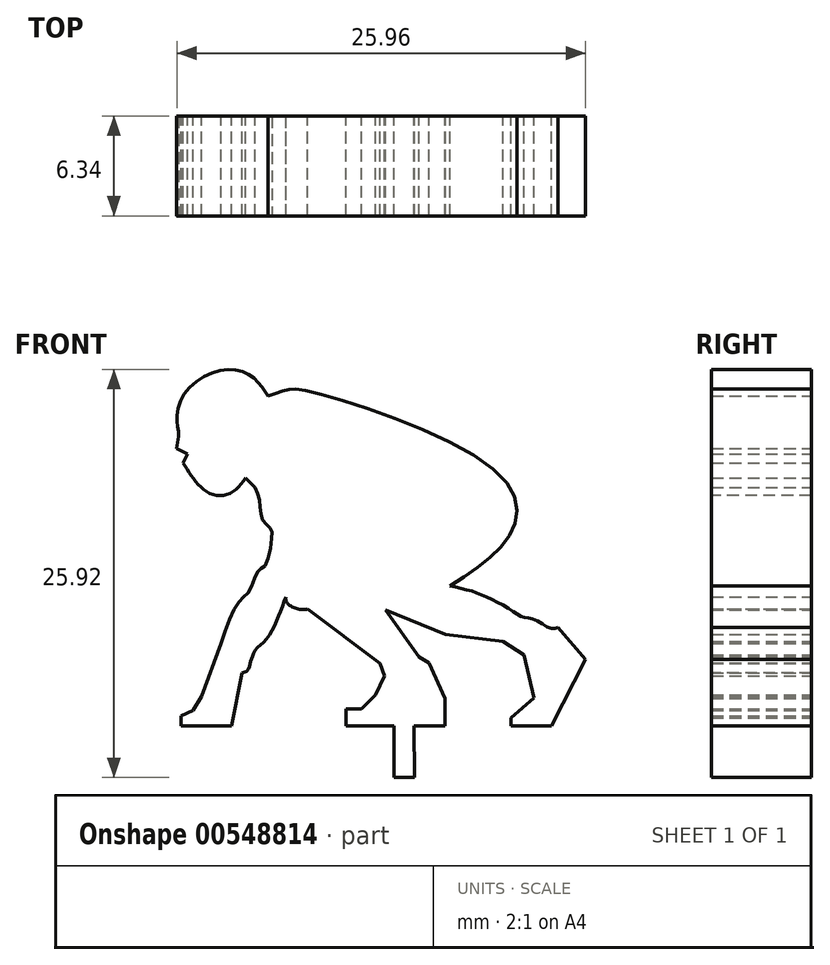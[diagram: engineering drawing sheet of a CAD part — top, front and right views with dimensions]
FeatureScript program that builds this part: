
annotation { "Feature Type Name" : "Feature", "Feature Type Description" : "" }
export const myFeature = defineFeature(function(context is Context, id is Id, definition is map)
    precondition{}
    {
        {
            var Q0;
            Q0=qCreatedBy(makeId("Front.planeOp"),FACE);
            var sketch = newSketch(context, id + "F0", { "sketchPlane" : qUnion([Q0])});
            skLineSegment(sketch, "E0", {"start": v(-11.37, -3.27) * mm, "end": v(-12.65, -3.27) * mm});
            skLineSegment(sketch, "E1", {"start": v(-12.65, -3.27) * mm, "end": v(-12.65, 0) * mm});
            skLineSegment(sketch, "E2", {"start": v(-12.65, 0) * mm, "end": v(-15.72, 0) * mm});
            skLineSegment(sketch, "E3", {"start": v(-15.72, 0) * mm, "end": v(-15.72, 1.09) * mm});
            skLineSegment(sketch, "E4", {"start": v(-15.72, 1.09) * mm, "end": v(-14.7, 1.09) * mm});
            skLineSegment(sketch, "E5", {"start": v(-14.7, 1.09) * mm, "end": v(-13.85, 1.97) * mm});
            skLineSegment(sketch, "E6", {"start": v(-13.85, 1.97) * mm, "end": v(-13.28, 3.19) * mm});
            skLineSegment(sketch, "E7", {"start": v(-13.28, 3.19) * mm, "end": v(-13.55, 3.98) * mm});
            skLineSegment(sketch, "E8", {"start": v(-13.55, 3.98) * mm, "end": v(-18.14, 7.43) * mm});
            skFitSpline(sketch, "E9", {"points": [v(-18.14, 7.43) * mm, v(-18.74, 7.43) * mm, v(-19.46, 7.83) * mm, v(-19.53, 8.2) * mm], "startDerivative": vector(-1.65, -0.23) * mm, "endDerivative": vector(0.09, 1.4) * mm});
            skFitSpline(sketch, "E10", {"points": [v(-19.53, 8.2) * mm, v(-20.08, 6.77) * mm, v(-20.8, 5.46) * mm, v(-21.47, 4.8) * mm, v(-21.7, 4.27) * mm, v(-21.82, 3.9) * mm, v(-21.97, 3.51) * mm, v(-22.32, 3.38) * mm, v(-22.32, 3.4) * mm], "startDerivative": vector(-2.6, -7.11) * mm, "endDerivative": vector(0.45, 1.13) * mm});
            skLineSegment(sketch, "E11", {"start": v(-22.32, 3.38) * mm, "end": v(-22.99, 0) * mm});
            skLineSegment(sketch, "E12", {"start": v(-22.99, 0) * mm, "end": v(-26.18, 0) * mm});
            skLineSegment(sketch, "E13", {"start": v(-26.18, 0) * mm, "end": v(-26.18, 0.65) * mm});
            skLineSegment(sketch, "E14", {"start": v(-26.18, 0.65) * mm, "end": v(-25.42, 1) * mm});
            skLineSegment(sketch, "E15", {"start": v(-25.42, 1) * mm, "end": v(-24.9, 1.86) * mm});
            skLineSegment(sketch, "E16", {"start": v(-24.9, 1.86) * mm, "end": v(-23.65, 5.23) * mm});
            skFitSpline(sketch, "E17", {"points": [v(-23.65, 5.23) * mm, v(-22.48, 7.91) * mm, v(-21.8, 8.6) * mm, v(-21.28, 9.87) * mm, v(-20.88, 10.15) * mm, v(-20.4, 12.04) * mm, v(-20.54, 12.6) * mm, v(-21.02, 13.11) * mm, v(-21.18, 14.2) * mm, v(-21.48, 15.15) * mm], "startDerivative": vector(6.31, 18.33) * mm, "endDerivative": vector(-3.63, 8.71) * mm});
            skLineSegment(sketch, "E18", {"start": v(-21.48, 15.15) * mm, "end": v(-22.08, 15.75) * mm});
            skFitSpline(sketch, "E19", {"points": [v(-22.08, 15.75) * mm, v(-23.04, 14.79) * mm, v(-24.22, 14.71) * mm, v(-25.25, 15.54) * mm, v(-26.07, 16.71) * mm], "startDerivative": vector(-3.44, -4.51) * mm, "endDerivative": vector(-2.96, 4.64) * mm});
            skLineSegment(sketch, "E20", {"start": v(-26.07, 16.71) * mm, "end": v(-25.78, 17.27) * mm});
            skLineSegment(sketch, "E21", {"start": v(-25.78, 17.27) * mm, "end": v(-26.45, 17.62) * mm});
            skFitSpline(sketch, "E22", {"points": [v(-26.45, 17.62) * mm, v(-26.35, 18.68) * mm, v(-26.45, 19.5) * mm, v(-25.96, 21.1) * mm, v(-24.04, 22.5) * mm, v(-22.23, 22.5) * mm, v(-21.22, 21.75) * mm, v(-20.66, 20.95) * mm], "startDerivative": vector(1.41, 8.93) * mm, "endDerivative": vector(4.2, -6.65) * mm});
            skFitSpline(sketch, "E23", {"points": [v(-20.66, 20.95) * mm, v(-19.54, 21.34) * mm, v(-18.14, 21.27) * mm, v(-5.9, 15.92) * mm, v(-5.29, 12.16) * mm, v(-9.11, 8.9) * mm], "startDerivative": vector(11.08, 4.16) * mm, "endDerivative": vector(-20.81, -13.46) * mm});
            skFitSpline(sketch, "E24", {"points": [v(-9.11, 8.9) * mm, v(-7.8, 8.58) * mm, v(-6.7, 8.15) * mm, v(-5.28, 7.41) * mm, v(-4.5, 6.92) * mm, v(-3.8, 6.79) * mm, v(-2.72, 6.21) * mm, v(-2.24, 6.27) * mm], "startDerivative": vector(8.42, -1.68) * mm, "endDerivative": vector(4.44, 1.66) * mm});
            skLineSegment(sketch, "E25", {"start": v(-2.24, 6.27) * mm, "end": v(-0.49, 4.22) * mm});
            skLineSegment(sketch, "E26", {"start": v(-0.49, 4.22) * mm, "end": v(-2.64, 0) * mm});
            skLineSegment(sketch, "E27", {"start": v(-2.64, 0) * mm, "end": v(-5.23, 0) * mm});
            skLineSegment(sketch, "E28", {"start": v(-5.23, 0) * mm, "end": v(-5.23, 0.52) * mm});
            skLineSegment(sketch, "E29", {"start": v(-5.23, 0.52) * mm, "end": v(-3.78, 1.8) * mm});
            skLineSegment(sketch, "E30", {"start": v(-3.78, 1.8) * mm, "end": v(-4.4, 4.52) * mm});
            skLineSegment(sketch, "E31", {"start": v(-4.4, 4.52) * mm, "end": v(-5.73, 5.37) * mm});
            skLineSegment(sketch, "E32", {"start": v(-5.73, 5.37) * mm, "end": v(-9.39, 5.8) * mm});
            skLineSegment(sketch, "E33", {"start": v(-9.39, 5.8) * mm, "end": v(-13.19, 7.39) * mm});
            skLineSegment(sketch, "E34", {"start": v(-13.19, 7.39) * mm, "end": v(-11.09, 4.39) * mm});
            skLineSegment(sketch, "E35", {"start": v(-11.09, 4.39) * mm, "end": v(-10.45, 4) * mm});
            skLineSegment(sketch, "E36", {"start": v(-10.45, 4) * mm, "end": v(-9.43, 1.74) * mm});
            skLineSegment(sketch, "E37", {"start": v(-9.43, 1.74) * mm, "end": v(-9.43, 0) * mm});
            skLineSegment(sketch, "E38", {"start": v(-9.43, 0) * mm, "end": v(-11.37, 0) * mm});
            skLineSegment(sketch, "E39", {"start": v(-11.37, 0) * mm, "end": v(-11.37, -3.27) * mm});
            skSolve(sketch);
        }
        {
            var Q0;
            Q0 = qSketchRegion(id + "F0", true);
            extrude(context, id + "F1", {"entities" : qUnion([Q0]), "depth" : 6.34 * mm, "offsetDistance" : 25 * mm});
        }
    });
